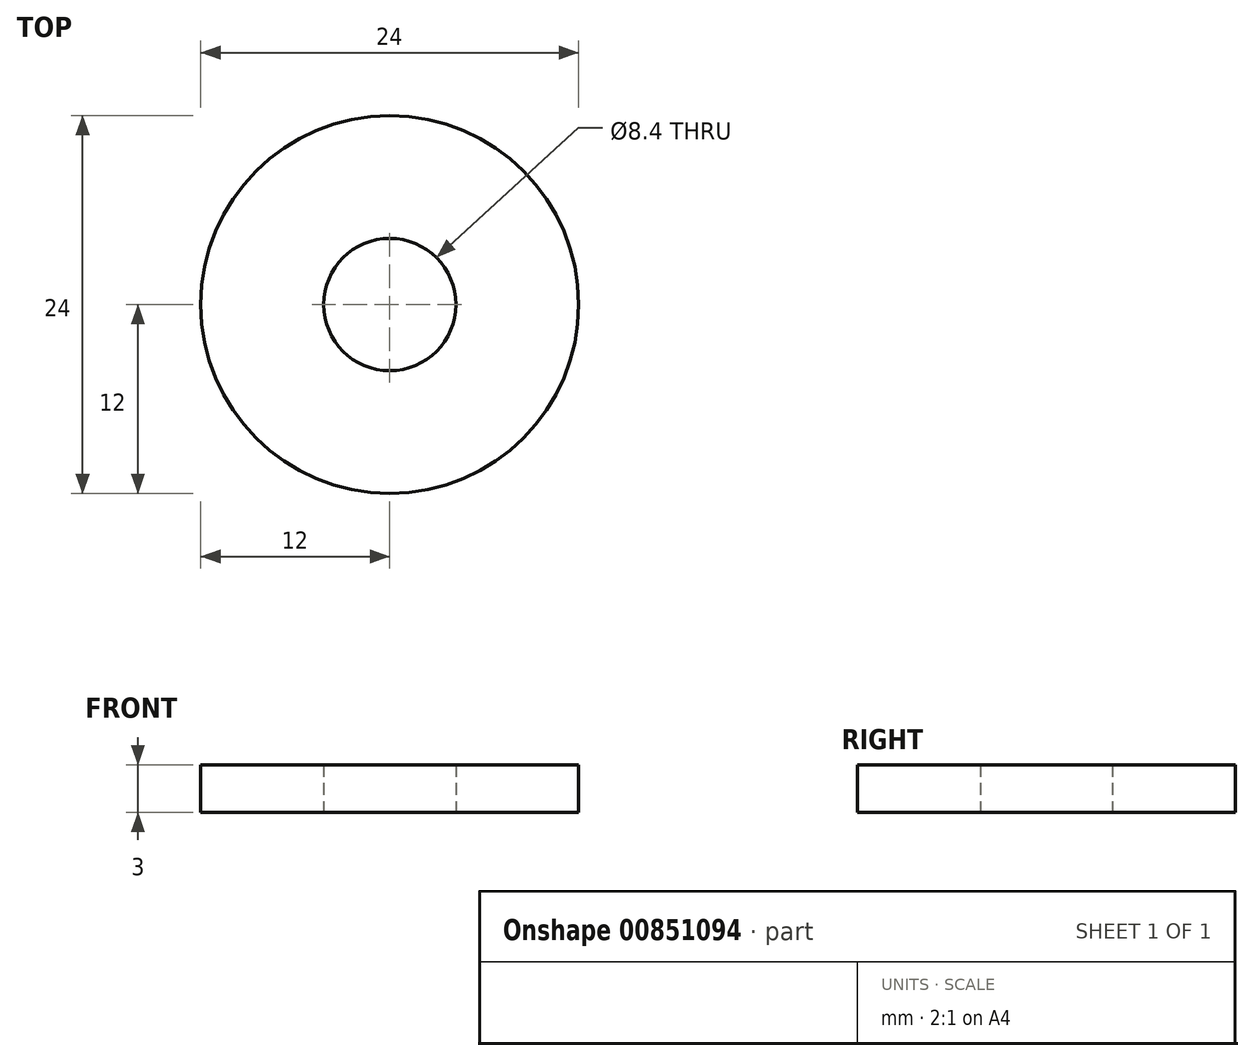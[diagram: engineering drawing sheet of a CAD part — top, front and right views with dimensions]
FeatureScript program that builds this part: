
annotation { "Feature Type Name" : "Feature", "Feature Type Description" : "" }
export const myFeature = defineFeature(function(context is Context, id is Id, definition is map)
    precondition{}
    {
        {
            var Q0;
            Q0=qCreatedBy(makeId("Top.planeOp"),FACE);
            var sketch = newSketch(context, id + "F0", { "sketchPlane" : qUnion([Q0])});
            skCircle(sketch, "E0", {"center": v(0, 0) * mm, "radius": 12 * mm});
            skCircle(sketch, "E1", {"center": v(0, 0) * mm, "radius": 4.2 * mm});
            skSolve(sketch);
        }
        {
            var Q0;
            Q0=makeQuery(id+"F0.imprint","IMPRINT",FACE,{"disambiguationData":[TD([[makeQuery(id+"F0.imprint","IMPRINT",EDGE,{"derivedFrom":sQuery(id+"F0.wireOp",EDGE,"E0")}),1.0]])]});
            extrude(context, id + "F1", {"entities" : qUnion([Q0]), "depth" : 3 * mm, "offsetDistance" : 25 * mm});
        }
    });
